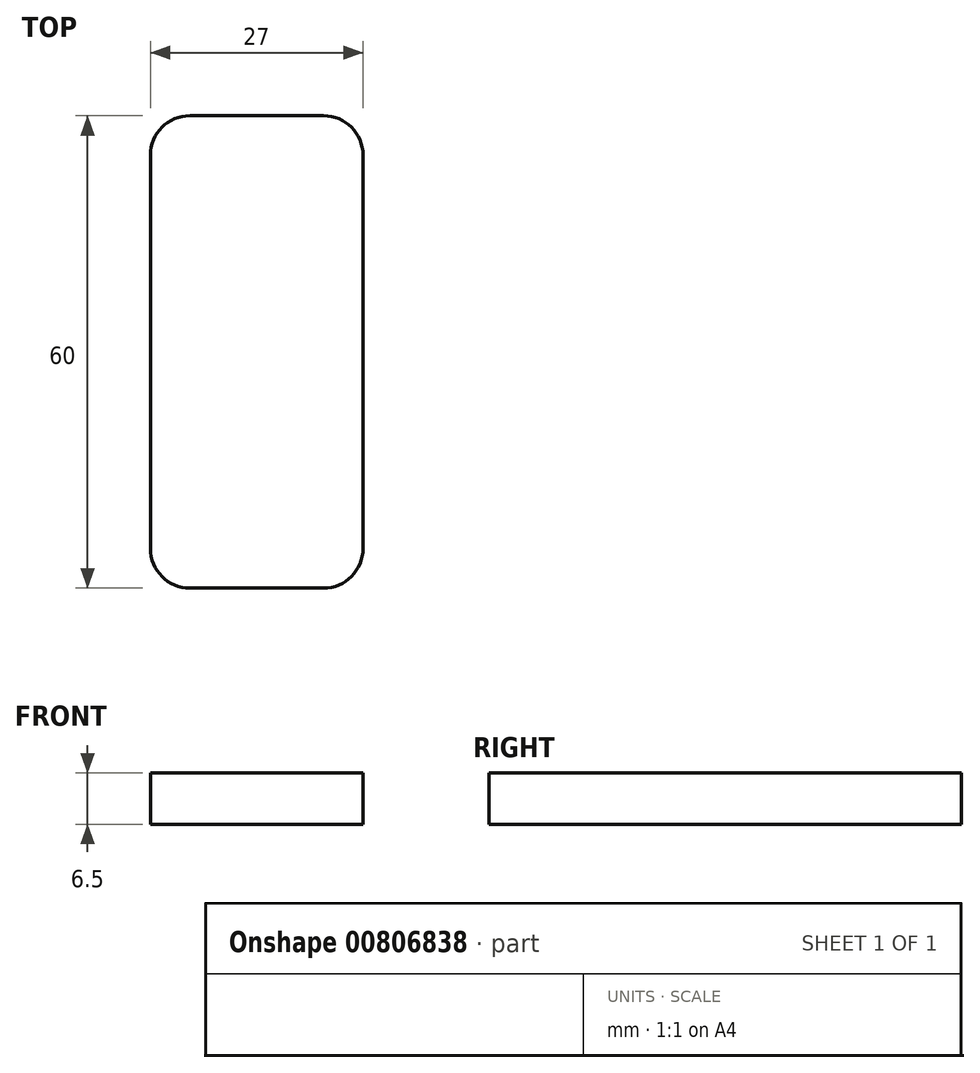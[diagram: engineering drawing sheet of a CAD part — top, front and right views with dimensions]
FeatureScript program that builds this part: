
annotation { "Feature Type Name" : "Feature", "Feature Type Description" : "" }
export const myFeature = defineFeature(function(context is Context, id is Id, definition is map)
    precondition{}
    {
        {
            var Q0;
            Q0=qCreatedBy(makeId("Top.planeOp"),FACE);
            var sketch = newSketch(context, id + "F0", { "sketchPlane" : qUnion([Q0])});
            skLineSegment(sketch, "E0.bottom", {"start": v(13.5, 30) * mm, "end": v(-13.5, 30) * mm});
            skLineSegment(sketch, "E0.top", {"start": v(13.5, -30) * mm, "end": v(-13.5, -30) * mm});
            skLineSegment(sketch, "E0.left", {"start": v(13.5, 30) * mm, "end": v(13.5, -30) * mm});
            skLineSegment(sketch, "E0.right", {"start": v(-13.5, 30) * mm, "end": v(-13.5, -30) * mm});
            skPoint(sketch, "E0.middle", {"position": v(0, 0) * mm});
            skSolve(sketch);
        }
        {
            var Q0;
            Q0 = qSketchRegion(id + "F0", true);
            extrude(context, id + "F1", {"entities" : qUnion([Q0]), "depth" : 6.5 * mm, "offsetDistance" : 25 * mm});
        }
        {
            var Q0;
            Q0=makeQuery(id+"F1.opExtrude","SWEPT_EDGE",EDGE,{"disambiguationData":[OSD([sQuery(id+"F0.wireOp",EDGE,"E0.top"),sQuery(id+"F0.wireOp",EDGE,"E0.left")])]});
            var Q1;
            Q1=makeQuery(id+"F1.opExtrude","SWEPT_EDGE",EDGE,{"disambiguationData":[OSD([sQuery(id+"F0.wireOp",EDGE,"E0.top"),sQuery(id+"F0.wireOp",EDGE,"E0.right")])]});
            var Q2;
            Q2=makeQuery(id+"F1.opExtrude","SWEPT_EDGE",EDGE,{"disambiguationData":[OSD([sQuery(id+"F0.wireOp",EDGE,"E0.bottom"),sQuery(id+"F0.wireOp",EDGE,"E0.left")])]});
            var Q3;
            Q3=makeQuery(id+"F1.opExtrude","SWEPT_EDGE",EDGE,{"disambiguationData":[OSD([sQuery(id+"F0.wireOp",EDGE,"E0.bottom"),sQuery(id+"F0.wireOp",EDGE,"E0.right")])]});
            fillet(context, id + "F2", {"entities" : qUnion([Q0, Q1, Q2, Q3]), "radius" : 5 * mm, "tangentPropagation" : true, "allowEdgeOverflow" : false});
        }
    });
